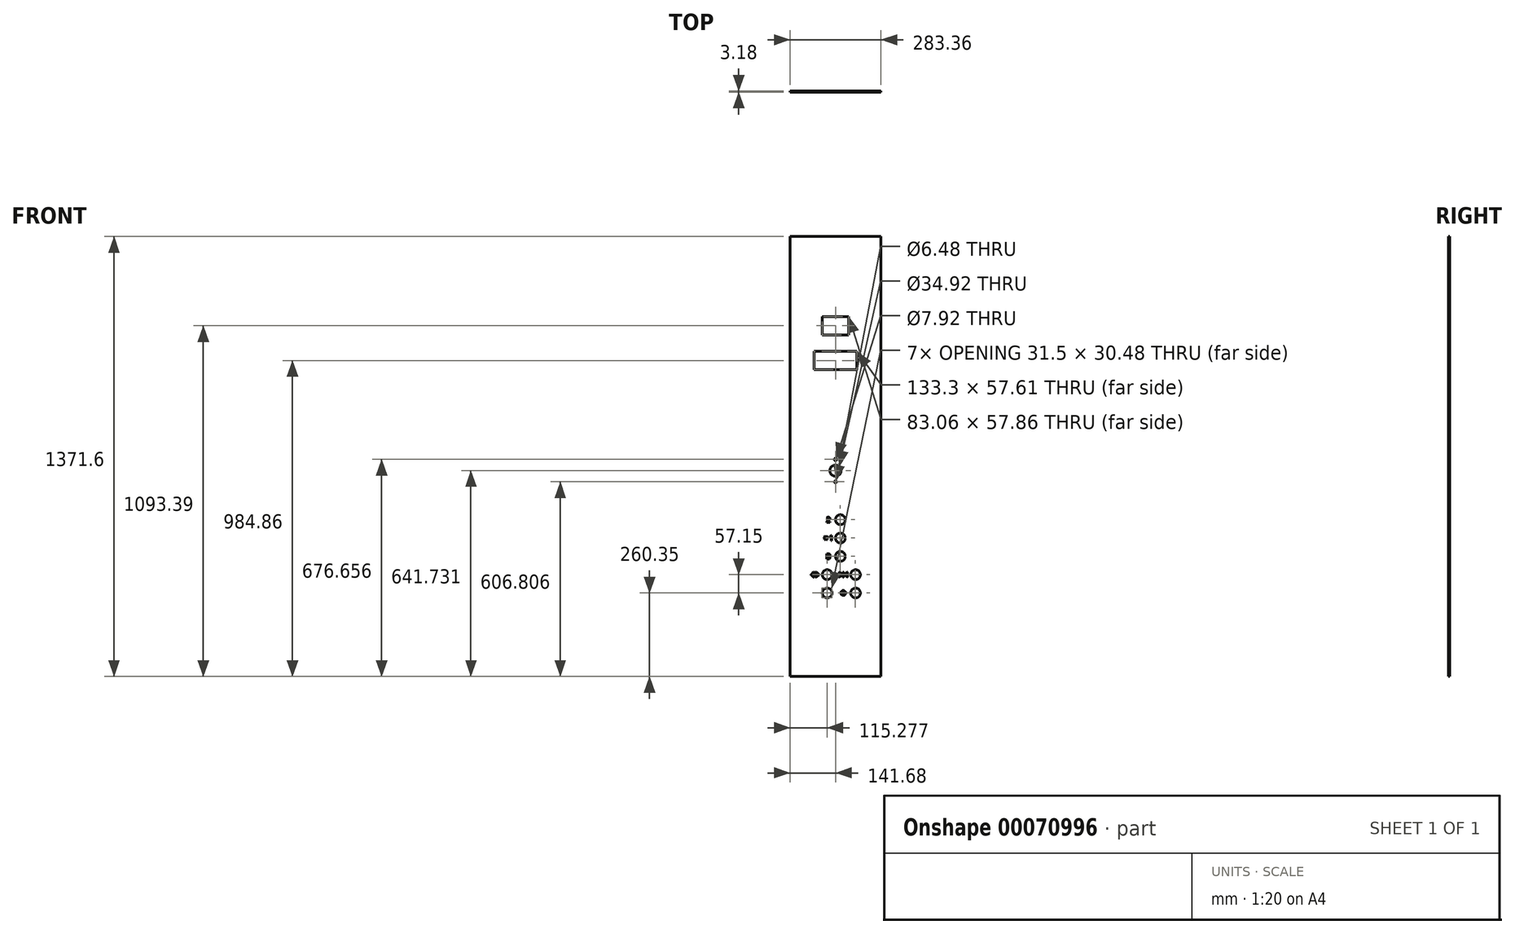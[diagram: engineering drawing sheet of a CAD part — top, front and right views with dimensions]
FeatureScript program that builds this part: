
annotation { "Feature Type Name" : "Feature", "Feature Type Description" : "" }
export const myFeature = defineFeature(function(context is Context, id is Id, definition is map)
    precondition{}
    {
        {
            var Q0;
            Q0=qCreatedBy(makeId("Front.planeOp"),FACE);
            var sketch = newSketch(context, id + "F0", { "sketchPlane" : qUnion([Q0])});
            skLineSegment(sketch, "E0.bottom", {"start": v(-141.68, 0) * mm, "end": v(141.68, 0) * mm});
            skLineSegment(sketch, "E0.top", {"start": v(-141.68, -1371.6) * mm, "end": v(141.68, -1371.6) * mm});
            skLineSegment(sketch, "E0.left", {"start": v(-141.68, 0) * mm, "end": v(-141.68, -1371.6) * mm});
            skLineSegment(sketch, "E0.right", {"start": v(141.68, 0) * mm, "end": v(141.68, -1371.6) * mm});
            skLineSegment(sketch, "E1", {"start": v(0, 0) * mm, "end": v(0, -1371.6) * mm, "construction": true});
            skLineSegment(sketch, "E2.bottom", {"start": v(-41.53, -249.28) * mm, "end": v(41.53, -249.28) * mm});
            skLineSegment(sketch, "E2.top", {"start": v(-41.53, -307.14) * mm, "end": v(41.53, -307.14) * mm});
            skLineSegment(sketch, "E2.left", {"start": v(-41.53, -249.28) * mm, "end": v(-41.53, -307.14) * mm});
            skLineSegment(sketch, "E2.right", {"start": v(41.53, -249.28) * mm, "end": v(41.53, -307.14) * mm});
            skLineSegment(sketch, "E3.bottom", {"start": v(-66.65, -357.94) * mm, "end": v(66.65, -357.94) * mm});
            skLineSegment(sketch, "E3.top", {"start": v(-66.65, -415.54) * mm, "end": v(66.65, -415.54) * mm});
            skLineSegment(sketch, "E3.left", {"start": v(-66.65, -357.94) * mm, "end": v(-66.65, -415.54) * mm});
            skLineSegment(sketch, "E3.right", {"start": v(66.65, -357.94) * mm, "end": v(66.65, -415.54) * mm});
            skArc(sketch, "E4", {"start": v(0.05, -883.86) * mm, "mid": v(30.5, -882.65) * mm, "end": v(0.05, -881.44) * mm});
            skPoint(sketch, "E5", {"position": v(0, -249.28) * mm});
            skPoint(sketch, "E6", {"position": v(0, -357.94) * mm});
            skArc(sketch, "E7", {"start": v(-0.16, -881.67) * mm, "mid": v(-1, -882.65) * mm, "end": v(-0.16, -883.63) * mm});
            skLineSegment(sketch, "E8", {"start": v(15.25, -882.65) * mm, "end": v(0, -882.65) * mm, "construction": true});
            skPoint(sketch, "E9.visualSharp", {"position": v(0.03, -881.66) * mm});
            skArc(sketch, "E9.filletArc", {"start": v(-0.16, -881.67) * mm, "mid": v(-0.02, -881.6) * mm, "end": v(0.05, -881.44) * mm});
            skPoint(sketch, "E10.visualSharp", {"position": v(0.03, -883.64) * mm});
            skArc(sketch, "E10.filletArc", {"start": v(0.05, -883.86) * mm, "mid": v(-0.02, -883.7) * mm, "end": v(-0.16, -883.63) * mm});
            skPoint(sketch, "E11.visualSharp", {"position": v(0.03, -940.8) * mm});
            skLineSegment(sketch, "E12", {"start": v(15.25, -939.8) * mm, "end": v(0, -939.8) * mm, "construction": true});
            skArc(sketch, "E13", {"start": v(0.05, -941) * mm, "mid": v(30.5, -939.8) * mm, "end": v(0.05, -938.6) * mm});
            skPoint(sketch, "E14.visualSharp", {"position": v(0.03, -938.8) * mm});
            skArc(sketch, "E14.filletArc", {"start": v(-0.16, -938.82) * mm, "mid": v(-0.02, -938.74) * mm, "end": v(0.05, -938.6) * mm});
            skArc(sketch, "E15", {"start": v(-0.16, -938.82) * mm, "mid": v(-1, -939.8) * mm, "end": v(-0.16, -940.78) * mm});
            skArc(sketch, "E11.filletArc", {"start": v(0.05, -941) * mm, "mid": v(-0.02, -940.86) * mm, "end": v(-0.16, -940.78) * mm});
            skPoint(sketch, "E16.visualSharp", {"position": v(0.03, -997.94) * mm});
            skLineSegment(sketch, "E17", {"start": v(15.25, -996.95) * mm, "end": v(0, -996.95) * mm, "construction": true});
            skArc(sketch, "E18", {"start": v(0.05, -998.16) * mm, "mid": v(30.5, -996.95) * mm, "end": v(0.05, -995.74) * mm});
            skPoint(sketch, "E19.visualSharp", {"position": v(0.03, -995.96) * mm});
            skArc(sketch, "E19.filletArc", {"start": v(-0.16, -995.97) * mm, "mid": v(-0.02, -995.9) * mm, "end": v(0.05, -995.74) * mm});
            skArc(sketch, "E20", {"start": v(-0.16, -995.97) * mm, "mid": v(-1, -996.95) * mm, "end": v(-0.16, -997.93) * mm});
            skArc(sketch, "E16.filletArc", {"start": v(0.05, -998.16) * mm, "mid": v(-0.02, -998) * mm, "end": v(-0.16, -997.93) * mm});
            skPoint(sketch, "E21.visualSharp", {"position": v(47.16, -1055.1) * mm});
            skLineSegment(sketch, "E22", {"start": v(62.38, -1054.1) * mm, "end": v(47.13, -1054.1) * mm, "construction": true});
            skArc(sketch, "E23", {"start": v(47.18, -1055.3) * mm, "mid": v(77.64, -1054.1) * mm, "end": v(47.18, -1052.9) * mm});
            skPoint(sketch, "E24.visualSharp", {"position": v(47.16, -1053.1) * mm});
            skArc(sketch, "E24.filletArc", {"start": v(46.97, -1053.12) * mm, "mid": v(47.11, -1053.04) * mm, "end": v(47.18, -1052.9) * mm});
            skArc(sketch, "E25", {"start": v(46.97, -1053.12) * mm, "mid": v(46.14, -1054.1) * mm, "end": v(46.97, -1055.08) * mm});
            skArc(sketch, "E21.filletArc", {"start": v(47.18, -1055.3) * mm, "mid": v(47.11, -1055.16) * mm, "end": v(46.97, -1055.08) * mm});
            skPoint(sketch, "E26.visualSharp", {"position": v(47.16, -1112.24) * mm});
            skLineSegment(sketch, "E27", {"start": v(62.38, -1111.25) * mm, "end": v(47.13, -1111.25) * mm, "construction": true});
            skArc(sketch, "E28", {"start": v(47.18, -1112.46) * mm, "mid": v(77.64, -1111.25) * mm, "end": v(47.18, -1110.04) * mm});
            skPoint(sketch, "E29.visualSharp", {"position": v(47.16, -1110.26) * mm});
            skArc(sketch, "E29.filletArc", {"start": v(46.97, -1110.27) * mm, "mid": v(47.11, -1110.2) * mm, "end": v(47.18, -1110.04) * mm});
            skArc(sketch, "E30", {"start": v(46.97, -1110.27) * mm, "mid": v(46.14, -1111.25) * mm, "end": v(46.97, -1112.23) * mm});
            skArc(sketch, "E26.filletArc", {"start": v(47.18, -1112.46) * mm, "mid": v(47.11, -1112.3) * mm, "end": v(46.97, -1112.23) * mm});
            skPoint(sketch, "E31.visualSharp", {"position": v(-41.13, -1055.1) * mm});
            skLineSegment(sketch, "E32", {"start": v(-25.9, -1054.1) * mm, "end": v(-41.16, -1054.1) * mm, "construction": true});
            skArc(sketch, "E33", {"start": v(-41.11, -1055.3) * mm, "mid": v(-10.66, -1054.1) * mm, "end": v(-41.11, -1052.9) * mm});
            skPoint(sketch, "E34.visualSharp", {"position": v(-41.13, -1053.1) * mm});
            skArc(sketch, "E34.filletArc", {"start": v(-41.32, -1053.12) * mm, "mid": v(-41.18, -1053.04) * mm, "end": v(-41.11, -1052.9) * mm});
            skArc(sketch, "E35", {"start": v(-41.32, -1053.12) * mm, "mid": v(-42.15, -1054.1) * mm, "end": v(-41.32, -1055.08) * mm});
            skArc(sketch, "E31.filletArc", {"start": v(-41.11, -1055.3) * mm, "mid": v(-41.18, -1055.16) * mm, "end": v(-41.32, -1055.08) * mm});
            skPoint(sketch, "E36.visualSharp", {"position": v(-41.13, -1112.24) * mm});
            skLineSegment(sketch, "E37", {"start": v(-25.9, -1111.25) * mm, "end": v(-41.16, -1111.25) * mm, "construction": true});
            skArc(sketch, "E38", {"start": v(-41.11, -1112.46) * mm, "mid": v(-10.66, -1111.25) * mm, "end": v(-41.11, -1110.04) * mm});
            skPoint(sketch, "E39.visualSharp", {"position": v(-41.13, -1110.26) * mm});
            skArc(sketch, "E39.filletArc", {"start": v(-41.32, -1110.27) * mm, "mid": v(-41.18, -1110.2) * mm, "end": v(-41.11, -1110.04) * mm});
            skArc(sketch, "E40", {"start": v(-41.32, -1110.27) * mm, "mid": v(-42.15, -1111.25) * mm, "end": v(-41.32, -1112.23) * mm});
            skArc(sketch, "E36.filletArc", {"start": v(-41.11, -1112.46) * mm, "mid": v(-41.18, -1112.3) * mm, "end": v(-41.32, -1112.23) * mm});
            skLineSegment(sketch, "E41.bottom", {"start": v(-141.68, -154.03) * mm, "end": v(141.68, -154.03) * mm, "construction": true});
            skLineSegment(sketch, "E41.top", {"start": v(-141.68, -1186.69) * mm, "end": v(141.68, -1186.69) * mm, "construction": true});
            skLineSegment(sketch, "E41.left", {"start": v(-141.68, -154.03) * mm, "end": v(-141.68, -1186.69) * mm, "construction": true});
            skLineSegment(sketch, "E41.right", {"start": v(141.68, -154.03) * mm, "end": v(141.68, -1186.69) * mm, "construction": true});
            skLineSegment(sketch, "E42", {"start": v(0, -154.03) * mm, "end": v(0, -1186.69) * mm, "construction": true});
            skCircle(sketch, "E43", {"center": v(0, -694.94) * mm, "radius": 3.96 * mm});
            skCircle(sketch, "E44", {"center": v(0, -729.87) * mm, "radius": 17.46 * mm});
            skCircle(sketch, "E45", {"center": v(0, -764.8) * mm, "radius": 3.24 * mm});
            skCircle(sketch, "E46", {"center": v(0, -806.07) * mm, "radius": 25.4 * mm, "construction": true});
            skText(sketch, "E47", { "text": "2", "fontName": "DroidSansMono.ttf"});
            skText(sketch, "E48", { "text": " 1", "fontName": "DroidSansMono.ttf"});
            skText(sketch, "E49", { "text": "B", "fontName": "DroidSansMono.ttf"});
            skLineSegment(sketch, "E50", {"start": v(-28.69, -882.65) * mm, "end": v(-17, -882.65) * mm, "construction": true});
            skCircle(sketch, "E51", {"center": v(-29.89, -939.8) * mm, "radius": 2.49 * mm, "construction": true});
            skLineSegment(sketch, "E52", {"start": v(-31.7, -937.31) * mm, "end": v(-28.08, -937.31) * mm, "construction": true});
            skLineSegment(sketch, "E53", {"start": v(-28.08, -937.31) * mm, "end": v(-26.96, -940.75) * mm, "construction": true});
            skLineSegment(sketch, "E54", {"start": v(-26.96, -940.75) * mm, "end": v(-29.89, -942.88) * mm, "construction": true});
            skLineSegment(sketch, "E55", {"start": v(-29.89, -942.88) * mm, "end": v(-32.81, -940.75) * mm, "construction": true});
            skLineSegment(sketch, "E56", {"start": v(-32.81, -940.75) * mm, "end": v(-31.7, -937.31) * mm, "construction": true});
            skLineSegment(sketch, "E57", {"start": v(-31.7, -937.31) * mm, "end": v(-29.89, -931.75) * mm});
            skLineSegment(sketch, "E58", {"start": v(-28.08, -937.31) * mm, "end": v(-29.89, -931.75) * mm});
            skLineSegment(sketch, "E59", {"start": v(-28.08, -937.31) * mm, "end": v(-22.23, -937.31) * mm});
            skLineSegment(sketch, "E60", {"start": v(-26.96, -940.75) * mm, "end": v(-22.23, -937.31) * mm});
            skLineSegment(sketch, "E61", {"start": v(-29.89, -942.88) * mm, "end": v(-25.16, -946.31) * mm});
            skLineSegment(sketch, "E62", {"start": v(-26.96, -940.75) * mm, "end": v(-25.16, -946.31) * mm});
            skLineSegment(sketch, "E63", {"start": v(-29.89, -942.88) * mm, "end": v(-34.62, -946.31) * mm});
            skLineSegment(sketch, "E64", {"start": v(-32.81, -940.75) * mm, "end": v(-34.62, -946.31) * mm});
            skLineSegment(sketch, "E65", {"start": v(-31.7, -937.31) * mm, "end": v(-37.55, -937.31) * mm});
            skLineSegment(sketch, "E66", {"start": v(-32.81, -940.75) * mm, "end": v(-37.55, -937.31) * mm});
            skCircle(sketch, "E67", {"center": v(-29.89, -939.8) * mm, "radius": 8.05 * mm, "construction": true});
            const initialGuessF0  = {"E47": [-0.02869, -0.8907, 1, 0, 0.0161], "E48": [-0.0337, -0.94785, 1, 0, 0.0161], "E49": [-0.02906, -1.005, 1, 0, 0.0161]};
            skSetInitialGuess(sketch, initialGuessF0);
            skSolve(sketch);
        }
        {
            var Q0;
            Q0=makeQuery(id+"F0.imprint","IMPRINT",FACE,{"disambiguationData":[TD([[makeQuery(id+"F0.imprint","IMPRINT",EDGE,{"derivedFrom":sQuery(id+"F0.wireOp",EDGE,"E0.bottom")}),-1.0]])]});
            var Q1;
            Q1=makeQuery(id+"F0.imprint","IMPRINT",FACE,{"disambiguationData":[TD([[makeQuery(id+"F0.imprint","IMPRINT",EDGE,{"derivedFrom":sQuery(id+"F0.wireOp",EDGE,"E49.sketch_text.stroke-11")}),1.0]])]});
            var Q2;
            Q2=makeQuery(id+"F0.imprint","IMPRINT",FACE,{"disambiguationData":[TD([[makeQuery(id+"F0.imprint","IMPRINT",EDGE,{"derivedFrom":sQuery(id+"F0.wireOp",EDGE,"E49.sketch_text.stroke-18")}),1.0]])]});
            extrude(context, id + "F1", {"entities" : qUnion([Q0, Q1, Q2]), "depth" : 3.17 * mm});
        }
        {
            var Q0;
            Q0=makeQuery(id+"F0.imprint","IMPRINT",FACE,{"disambiguationData":[TD([[makeQuery(id+"F0.imprint","IMPRINT",EDGE,{"derivedFrom":sQuery(id+"F0.wireOp",EDGE,"E49.sketch_text.stroke-0")}),-1.0]])]});
            var Q1;
            Q1=makeQuery(id+"F0.imprint","IMPRINT",FACE,{"disambiguationData":[TD([[makeQuery(id+"F0.imprint","IMPRINT",EDGE,{"derivedFrom":sQuery(id+"F0.wireOp",EDGE,"E57")}),-1.0]])]});
            var Q2;
            Q2=makeQuery(id+"F0.imprint","IMPRINT",FACE,{"disambiguationData":[TD([[makeQuery(id+"F0.imprint","IMPRINT",EDGE,{"derivedFrom":sQuery(id+"F0.wireOp",EDGE,"E48.sketch_text.stroke-0")}),-1.0]])]});
            var Q3;
            Q3=makeQuery(id+"F0.imprint","IMPRINT",FACE,{"disambiguationData":[TD([[makeQuery(id+"F0.imprint","IMPRINT",EDGE,{"derivedFrom":sQuery(id+"F0.wireOp",EDGE,"E47.sketch_text.stroke-0")}),-1.0]])]});
            extrude(context, id + "F2", {"entities" : qUnion([Q0, Q1, Q2, Q3]), "operationType" : NewBodyOperationType.ADD, "depth" : 2.92 * mm});
        }
        {
            var Q0;
            Q0=makeQuery(id+"F1.opExtrude","CAP_FACE",FACE,{"disambiguationData":[OSD([sQuery(id+"F0.wireOp",EDGE,"E0.bottom"),sQuery(id+"F0.wireOp",EDGE,"E0.top"),sQuery(id+"F0.wireOp",EDGE,"E0.left"),sQuery(id+"F0.wireOp",EDGE,"E0.right"),sQuery(id+"F0.wireOp",EDGE,"E2.bottom"),sQuery(id+"F0.wireOp",EDGE,"E2.top"),sQuery(id+"F0.wireOp",EDGE,"E2.left"),sQuery(id+"F0.wireOp",EDGE,"E2.right"),sQuery(id+"F0.wireOp",EDGE,"E3.bottom"),sQuery(id+"F0.wireOp",EDGE,"E3.top"),sQuery(id+"F0.wireOp",EDGE,"E3.left"),sQuery(id+"F0.wireOp",EDGE,"E3.right"),sQuery(id+"F0.wireOp",EDGE,"E4"),sQuery(id+"F0.wireOp",EDGE,"E7"),sQuery(id+"F0.wireOp",EDGE,"E9.filletArc"),sQuery(id+"F0.wireOp",EDGE,"E10.filletArc"),sQuery(id+"F0.wireOp",EDGE,"E13"),sQuery(id+"F0.wireOp",EDGE,"E14.filletArc"),sQuery(id+"F0.wireOp",EDGE,"E15"),sQuery(id+"F0.wireOp",EDGE,"E11.filletArc"),sQuery(id+"F0.wireOp",EDGE,"E18"),sQuery(id+"F0.wireOp",EDGE,"E19.filletArc"),sQuery(id+"F0.wireOp",EDGE,"E20"),sQuery(id+"F0.wireOp",EDGE,"E16.filletArc"),sQuery(id+"F0.wireOp",EDGE,"E23"),sQuery(id+"F0.wireOp",EDGE,"E24.filletArc"),sQuery(id+"F0.wireOp",EDGE,"E25"),sQuery(id+"F0.wireOp",EDGE,"E21.filletArc"),sQuery(id+"F0.wireOp",EDGE,"E28"),sQuery(id+"F0.wireOp",EDGE,"E29.filletArc"),sQuery(id+"F0.wireOp",EDGE,"E30"),sQuery(id+"F0.wireOp",EDGE,"E26.filletArc"),sQuery(id+"F0.wireOp",EDGE,"E33"),sQuery(id+"F0.wireOp",EDGE,"E34.filletArc"),sQuery(id+"F0.wireOp",EDGE,"E35"),sQuery(id+"F0.wireOp",EDGE,"E31.filletArc"),sQuery(id+"F0.wireOp",EDGE,"E38"),sQuery(id+"F0.wireOp",EDGE,"E39.filletArc"),sQuery(id+"F0.wireOp",EDGE,"E40"),sQuery(id+"F0.wireOp",EDGE,"E36.filletArc"),sQuery(id+"F0.wireOp",EDGE,"E43"),sQuery(id+"F0.wireOp",EDGE,"E44"),sQuery(id+"F0.wireOp",EDGE,"E45")])],"isStart":false});
            var sketch = newSketch(context, id + "F3", { "sketchPlane" : qUnion([Q0])});
            skText(sketch, "E68", { "text": "2", "fontName": "DroidSansMono.ttf"});
            skText(sketch, "E69", { "text": " 1", "fontName": "DroidSansMono.ttf"});
            skText(sketch, "E70", { "text": "B", "fontName": "DroidSansMono.ttf"});
            skLineSegment(sketch, "E71", {"start": v(-28.69, -882.65) * mm, "end": v(-17, -882.65) * mm, "construction": true});
            skCircle(sketch, "E72", {"center": v(-29.89, -939.8) * mm, "radius": 2.49 * mm, "construction": true});
            skLineSegment(sketch, "E73", {"start": v(-31.7, -937.31) * mm, "end": v(-28.08, -937.31) * mm, "construction": true});
            skLineSegment(sketch, "E74", {"start": v(-28.08, -937.31) * mm, "end": v(-26.96, -940.75) * mm, "construction": true});
            skLineSegment(sketch, "E75", {"start": v(-26.96, -940.75) * mm, "end": v(-29.89, -942.88) * mm, "construction": true});
            skLineSegment(sketch, "E76", {"start": v(-29.89, -942.88) * mm, "end": v(-32.81, -940.75) * mm, "construction": true});
            skLineSegment(sketch, "E77", {"start": v(-32.81, -940.75) * mm, "end": v(-31.7, -937.31) * mm, "construction": true});
            skLineSegment(sketch, "E78", {"start": v(-31.7, -937.31) * mm, "end": v(-29.89, -931.75) * mm});
            skLineSegment(sketch, "E79", {"start": v(-28.08, -937.31) * mm, "end": v(-29.89, -931.75) * mm});
            skLineSegment(sketch, "E80", {"start": v(-28.08, -937.31) * mm, "end": v(-22.23, -937.31) * mm});
            skLineSegment(sketch, "E81", {"start": v(-26.96, -940.75) * mm, "end": v(-22.23, -937.31) * mm});
            skLineSegment(sketch, "E82", {"start": v(-29.89, -942.88) * mm, "end": v(-25.16, -946.31) * mm});
            skLineSegment(sketch, "E83", {"start": v(-26.96, -940.75) * mm, "end": v(-25.16, -946.31) * mm});
            skLineSegment(sketch, "E84", {"start": v(-29.89, -942.88) * mm, "end": v(-34.62, -946.31) * mm});
            skLineSegment(sketch, "E85", {"start": v(-32.81, -940.75) * mm, "end": v(-34.62, -946.31) * mm});
            skLineSegment(sketch, "E86", {"start": v(-31.7, -937.31) * mm, "end": v(-37.55, -937.31) * mm});
            skLineSegment(sketch, "E87", {"start": v(-32.81, -940.75) * mm, "end": v(-37.55, -937.31) * mm});
            skCircle(sketch, "E88", {"center": v(-29.89, -939.8) * mm, "radius": 8.05 * mm, "construction": true});
            skLineSegment(sketch, "E89.bottom", {"start": v(-76.7, -1046.11) * mm, "end": v(-51.3, -1046.11) * mm, "construction": true});
            skLineSegment(sketch, "E89.top", {"start": v(-76.7, -1062.09) * mm, "end": v(-51.3, -1062.09) * mm, "construction": true});
            skLineSegment(sketch, "E89.left", {"start": v(-76.7, -1046.11) * mm, "end": v(-76.7, -1062.09) * mm, "construction": true});
            skLineSegment(sketch, "E89.right", {"start": v(-51.3, -1046.11) * mm, "end": v(-51.3, -1062.09) * mm, "construction": true});
            skLineSegment(sketch, "E90", {"start": v(-69.07, -1046.3) * mm, "end": v(-76.27, -1053.66) * mm});
            skLineSegment(sketch, "E91", {"start": v(-76.27, -1054.54) * mm, "end": v(-69.07, -1061.9) * mm});
            skLineSegment(sketch, "E92", {"start": v(-67.98, -1061.45) * mm, "end": v(-67.98, -1046.75) * mm});
            skLineSegment(sketch, "E93", {"start": v(-60.04, -1046.75) * mm, "end": v(-60.04, -1061.45) * mm});
            skLineSegment(sketch, "E94", {"start": v(-58.95, -1061.9) * mm, "end": v(-51.74, -1054.54) * mm});
            skLineSegment(sketch, "E95", {"start": v(-51.74, -1053.66) * mm, "end": v(-58.95, -1046.3) * mm});
            skLineSegment(sketch, "E96", {"start": v(-64.8, -1046.75) * mm, "end": v(-64.8, -1061.45) * mm});
            skLineSegment(sketch, "E97", {"start": v(-64.17, -1062.09) * mm, "end": v(-63.85, -1062.09) * mm});
            skLineSegment(sketch, "E98", {"start": v(-63.21, -1061.45) * mm, "end": v(-63.21, -1046.75) * mm});
            skLineSegment(sketch, "E99", {"start": v(-63.85, -1046.11) * mm, "end": v(-64.17, -1046.11) * mm});
            skLineSegment(sketch, "E100", {"start": v(-74.05, -1053.66) * mm, "end": v(-70.65, -1050.19) * mm});
            skLineSegment(sketch, "E101", {"start": v(-69.56, -1050.63) * mm, "end": v(-69.56, -1057.57) * mm});
            skLineSegment(sketch, "E102", {"start": v(-70.65, -1058.01) * mm, "end": v(-74.05, -1054.54) * mm});
            skLineSegment(sketch, "E103", {"start": v(-58.45, -1050.63) * mm, "end": v(-58.45, -1057.57) * mm});
            skLineSegment(sketch, "E104", {"start": v(-57.36, -1058.01) * mm, "end": v(-53.97, -1054.54) * mm});
            skLineSegment(sketch, "E105", {"start": v(-53.97, -1053.66) * mm, "end": v(-57.36, -1050.19) * mm});
            skLineSegment(sketch, "E106", {"start": v(-76.7, -1054.1) * mm, "end": v(-51.3, -1054.1) * mm, "construction": true});
            skPoint(sketch, "E107.visualSharp", {"position": v(-67.98, -1045.2) * mm});
            skArc(sketch, "E107.filletArc", {"start": v(-67.98, -1046.75) * mm, "mid": v(-68.37, -1046.16) * mm, "end": v(-69.07, -1046.3) * mm});
            skPoint(sketch, "E108.visualSharp", {"position": v(-69.56, -1049.08) * mm});
            skArc(sketch, "E108.filletArc", {"start": v(-69.56, -1050.63) * mm, "mid": v(-69.96, -1050.05) * mm, "end": v(-70.65, -1050.19) * mm});
            skPoint(sketch, "E109.visualSharp", {"position": v(-76.7, -1054.1) * mm});
            skArc(sketch, "E109.filletArc", {"start": v(-76.27, -1053.66) * mm, "mid": v(-76.45, -1054.1) * mm, "end": v(-76.27, -1054.54) * mm});
            skPoint(sketch, "E110.visualSharp", {"position": v(-74.49, -1054.1) * mm});
            skArc(sketch, "E110.filletArc", {"start": v(-74.05, -1053.66) * mm, "mid": v(-74.23, -1054.1) * mm, "end": v(-74.05, -1054.54) * mm});
            skPoint(sketch, "E111.visualSharp", {"position": v(-67.98, -1063) * mm});
            skArc(sketch, "E111.filletArc", {"start": v(-69.07, -1061.9) * mm, "mid": v(-68.37, -1062.04) * mm, "end": v(-67.98, -1061.45) * mm});
            skPoint(sketch, "E112.visualSharp", {"position": v(-69.56, -1059.12) * mm});
            skArc(sketch, "E112.filletArc", {"start": v(-70.65, -1058.01) * mm, "mid": v(-69.96, -1058.15) * mm, "end": v(-69.56, -1057.57) * mm});
            skPoint(sketch, "E113.visualSharp", {"position": v(-64.8, -1046.11) * mm});
            skArc(sketch, "E113.filletArc", {"start": v(-64.17, -1046.11) * mm, "mid": v(-64.62, -1046.3) * mm, "end": v(-64.8, -1046.75) * mm});
            skPoint(sketch, "E114.visualSharp", {"position": v(-63.21, -1046.11) * mm});
            skArc(sketch, "E114.filletArc", {"start": v(-63.21, -1046.75) * mm, "mid": v(-63.4, -1046.3) * mm, "end": v(-63.85, -1046.11) * mm});
            skPoint(sketch, "E115.visualSharp", {"position": v(-64.8, -1062.09) * mm});
            skArc(sketch, "E115.filletArc", {"start": v(-64.8, -1061.45) * mm, "mid": v(-64.62, -1061.9) * mm, "end": v(-64.17, -1062.09) * mm});
            skPoint(sketch, "E116.visualSharp", {"position": v(-63.21, -1062.09) * mm});
            skArc(sketch, "E116.filletArc", {"start": v(-63.85, -1062.09) * mm, "mid": v(-63.4, -1061.9) * mm, "end": v(-63.21, -1061.45) * mm});
            skPoint(sketch, "E117.visualSharp", {"position": v(-60.04, -1063) * mm});
            skArc(sketch, "E117.filletArc", {"start": v(-60.04, -1061.45) * mm, "mid": v(-59.64, -1062.04) * mm, "end": v(-58.95, -1061.9) * mm});
            skPoint(sketch, "E118.visualSharp", {"position": v(-58.45, -1059.12) * mm});
            skArc(sketch, "E118.filletArc", {"start": v(-58.45, -1057.57) * mm, "mid": v(-58.06, -1058.15) * mm, "end": v(-57.36, -1058.01) * mm});
            skPoint(sketch, "E119.visualSharp", {"position": v(-58.45, -1049.08) * mm});
            skArc(sketch, "E119.filletArc", {"start": v(-57.36, -1050.19) * mm, "mid": v(-58.06, -1050.05) * mm, "end": v(-58.45, -1050.63) * mm});
            skPoint(sketch, "E120.visualSharp", {"position": v(-60.04, -1045.2) * mm});
            skArc(sketch, "E120.filletArc", {"start": v(-58.95, -1046.3) * mm, "mid": v(-59.64, -1046.16) * mm, "end": v(-60.04, -1046.75) * mm});
            skPoint(sketch, "E121.visualSharp", {"position": v(-51.3, -1054.1) * mm});
            skArc(sketch, "E121.filletArc", {"start": v(-51.74, -1054.54) * mm, "mid": v(-51.56, -1054.1) * mm, "end": v(-51.74, -1053.66) * mm});
            skPoint(sketch, "E122.visualSharp", {"position": v(-53.53, -1054.1) * mm});
            skArc(sketch, "E122.filletArc", {"start": v(-53.97, -1054.54) * mm, "mid": v(-53.79, -1054.1) * mm, "end": v(-53.97, -1053.66) * mm});
            skLineSegment(sketch, "E123", {"start": v(-72.35, -1051.92) * mm, "end": v(-73.48, -1050.81) * mm, "construction": true});
            skLineSegment(sketch, "E124", {"start": v(-69.56, -1050.63) * mm, "end": v(-67.98, -1050.63) * mm, "construction": true});
            skLineSegment(sketch, "E125", {"start": v(-55.66, -1051.92) * mm, "end": v(-54.53, -1050.81) * mm, "construction": true});
            skLineSegment(sketch, "E126", {"start": v(-64.8, -1046.75) * mm, "end": v(-63.21, -1046.75) * mm, "construction": true});
            skLineSegment(sketch, "E127", {"start": v(-60.04, -1050.63) * mm, "end": v(-58.45, -1050.63) * mm, "construction": true});
            skLineSegment(sketch, "E128", {"start": v(-67.98, -1046.75) * mm, "end": v(-64.8, -1046.75) * mm, "construction": true});
            skLineSegment(sketch, "E129", {"start": v(-63.21, -1046.75) * mm, "end": v(-60.04, -1046.75) * mm, "construction": true});
            skLineSegment(sketch, "E130", {"start": v(-64, -1046.11) * mm, "end": v(-64, -1062.09) * mm, "construction": true});
            skPoint(sketch, "E131.visualSharp", {"position": v(20.58, -1054.1) * mm});
            skLineSegment(sketch, "E132", {"start": v(36.98, -1061.45) * mm, "end": v(36.98, -1046.75) * mm});
            skPoint(sketch, "E133.visualSharp", {"position": v(35.4, -1049.02) * mm});
            skLineSegment(sketch, "E134", {"start": v(35.4, -1050.54) * mm, "end": v(35.4, -1057.66) * mm});
            skLineSegment(sketch, "E135", {"start": v(20.58, -1054.1) * mm, "end": v(27.98, -1054.1) * mm, "construction": true});
            skPoint(sketch, "E136.visualSharp", {"position": v(11.58, -1045.23) * mm});
            skPoint(sketch, "E137.visualSharp", {"position": v(35.4, -1059.18) * mm});
            skLineSegment(sketch, "E138", {"start": v(28.44, -1054.55) * mm, "end": v(35.9, -1061.9) * mm});
            skPoint(sketch, "E139.visualSharp", {"position": v(11.58, -1062.97) * mm});
            skPoint(sketch, "E140.visualSharp", {"position": v(27.98, -1054.1) * mm});
            skLineSegment(sketch, "E141", {"start": v(11.58, -1046.75) * mm, "end": v(11.58, -1061.45) * mm});
            skLineSegment(sketch, "E142", {"start": v(25.08, -1061.45) * mm, "end": v(25.08, -1046.75) * mm});
            skPoint(sketch, "E143.visualSharp", {"position": v(36.98, -1062.97) * mm});
            skPoint(sketch, "E144.visualSharp", {"position": v(13.17, -1049.02) * mm});
            skLineSegment(sketch, "E145", {"start": v(12.66, -1061.9) * mm, "end": v(20.12, -1054.55) * mm});
            skPoint(sketch, "E146.visualSharp", {"position": v(13.17, -1059.18) * mm});
            skPoint(sketch, "E147.visualSharp", {"position": v(30.24, -1054.1) * mm});
            skLineSegment(sketch, "E148", {"start": v(13.17, -1050.54) * mm, "end": v(13.17, -1057.66) * mm});
            skLineSegment(sketch, "E149", {"start": v(23.49, -1046.75) * mm, "end": v(23.49, -1061.45) * mm});
            skPoint(sketch, "E150.visualSharp", {"position": v(18.32, -1054.1) * mm});
            skPoint(sketch, "E151.visualSharp", {"position": v(23.49, -1060.36) * mm});
            skPoint(sketch, "E152.visualSharp", {"position": v(36.98, -1045.23) * mm});
            skPoint(sketch, "E153.visualSharp", {"position": v(25.08, -1060.36) * mm});
            skLineSegment(sketch, "E154", {"start": v(35.9, -1046.3) * mm, "end": v(28.44, -1053.65) * mm});
            skPoint(sketch, "E155.visualSharp", {"position": v(23.49, -1044.39) * mm});
            skLineSegment(sketch, "E156", {"start": v(20.12, -1053.65) * mm, "end": v(12.66, -1046.3) * mm});
            skPoint(sketch, "E157.visualSharp", {"position": v(25.08, -1044.39) * mm});
            skArc(sketch, "E146.filletArc", {"start": v(13.17, -1057.66) * mm, "mid": v(13.56, -1058.25) * mm, "end": v(14.25, -1058.11) * mm});
            skLineSegment(sketch, "E158", {"start": v(16.06, -1051.87) * mm, "end": v(17.17, -1050.74) * mm, "construction": true});
            skLineSegment(sketch, "E159", {"start": v(34.31, -1058.11) * mm, "end": v(30.7, -1054.55) * mm});
            skArc(sketch, "E137.filletArc", {"start": v(34.31, -1058.11) * mm, "mid": v(35, -1058.25) * mm, "end": v(35.4, -1057.66) * mm});
            skLineSegment(sketch, "E160", {"start": v(14.25, -1058.11) * mm, "end": v(17.86, -1054.55) * mm});
            skArc(sketch, "E140.filletArc", {"start": v(28.44, -1053.65) * mm, "mid": v(28.25, -1054.1) * mm, "end": v(28.44, -1054.55) * mm});
            skArc(sketch, "E150.filletArc", {"start": v(17.86, -1054.55) * mm, "mid": v(18.05, -1054.1) * mm, "end": v(17.86, -1053.65) * mm});
            skLineSegment(sketch, "E161", {"start": v(30.7, -1053.65) * mm, "end": v(34.31, -1050.09) * mm});
            skLineSegment(sketch, "E162", {"start": v(32.5, -1051.87) * mm, "end": v(31.4, -1050.74) * mm, "construction": true});
            skLineSegment(sketch, "E163", {"start": v(35.4, -1050.54) * mm, "end": v(36.98, -1050.54) * mm, "construction": true});
            skArc(sketch, "E133.filletArc", {"start": v(35.4, -1050.54) * mm, "mid": v(35, -1049.95) * mm, "end": v(34.31, -1050.09) * mm});
            skLineSegment(sketch, "E164", {"start": v(17.86, -1053.65) * mm, "end": v(14.25, -1050.09) * mm});
            skArc(sketch, "E131.filletArc", {"start": v(20.12, -1054.55) * mm, "mid": v(20.31, -1054.1) * mm, "end": v(20.12, -1053.65) * mm});
            skArc(sketch, "E147.filletArc", {"start": v(30.7, -1053.65) * mm, "mid": v(30.51, -1054.1) * mm, "end": v(30.7, -1054.55) * mm});
            skArc(sketch, "E144.filletArc", {"start": v(14.25, -1050.09) * mm, "mid": v(13.56, -1049.95) * mm, "end": v(13.17, -1050.54) * mm});
            skArc(sketch, "E143.filletArc", {"start": v(35.9, -1061.9) * mm, "mid": v(36.6, -1062.04) * mm, "end": v(36.98, -1061.45) * mm});
            skLineSegment(sketch, "E165", {"start": v(11.58, -1050.54) * mm, "end": v(13.17, -1050.54) * mm, "construction": true});
            skArc(sketch, "E139.filletArc", {"start": v(11.58, -1061.45) * mm, "mid": v(11.97, -1062.04) * mm, "end": v(12.66, -1061.9) * mm});
            skArc(sketch, "E136.filletArc", {"start": v(12.66, -1046.3) * mm, "mid": v(11.97, -1046.16) * mm, "end": v(11.58, -1046.75) * mm});
            skArc(sketch, "E151.filletArc", {"start": v(23.49, -1061.45) * mm, "mid": v(23.67, -1061.9) * mm, "end": v(24.12, -1062.09) * mm});
            skArc(sketch, "E153.filletArc", {"start": v(24.44, -1062.09) * mm, "mid": v(24.9, -1061.9) * mm, "end": v(25.08, -1061.45) * mm});
            skArc(sketch, "E152.filletArc", {"start": v(36.98, -1046.75) * mm, "mid": v(36.6, -1046.16) * mm, "end": v(35.9, -1046.3) * mm});
            skArc(sketch, "E157.filletArc", {"start": v(25.08, -1046.75) * mm, "mid": v(24.9, -1046.3) * mm, "end": v(24.44, -1046.11) * mm});
            skLineSegment(sketch, "E166", {"start": v(23.49, -1046.75) * mm, "end": v(25.08, -1046.75) * mm, "construction": true});
            skArc(sketch, "E155.filletArc", {"start": v(24.12, -1046.11) * mm, "mid": v(23.67, -1046.3) * mm, "end": v(23.49, -1046.75) * mm});
            skLineSegment(sketch, "E167", {"start": v(24.12, -1046.11) * mm, "end": v(24.44, -1046.11) * mm});
            skLineSegment(sketch, "E168", {"start": v(24.12, -1062.09) * mm, "end": v(24.44, -1062.09) * mm});
            skLineSegment(sketch, "E169", {"start": v(20.31, -1050.1) * mm, "end": v(20.31, -1055.92) * mm, "construction": true});
            skLineSegment(sketch, "E170", {"start": v(28.25, -1049.84) * mm, "end": v(28.25, -1055.9) * mm, "construction": true});
            skLineSegment(sketch, "E171", {"start": v(24.28, -1042.27) * mm, "end": v(24.28, -1076.34) * mm, "construction": true});
            skPoint(sketch, "E171.endSnap0", {"position": v(24.28, -1054.1) * mm});
            skLineSegment(sketch, "E172", {"start": v(11.58, -1054.1) * mm, "end": v(36.98, -1054.1) * mm, "construction": true});
            skCircle(sketch, "E173.cCircle", {"center": v(24.28, -1111.25) * mm, "radius": 7.99 * mm, "construction": true});
            skLineSegment(sketch, "E173.0", {"start": v(27.53, -1104.06) * mm, "end": v(31.48, -1108) * mm});
            skLineSegment(sketch, "E173.1", {"start": v(31.66, -1108.46) * mm, "end": v(31.66, -1114.04) * mm});
            skLineSegment(sketch, "E173.2", {"start": v(31.48, -1114.5) * mm, "end": v(27.53, -1118.44) * mm});
            skLineSegment(sketch, "E173.3", {"start": v(27.08, -1118.63) * mm, "end": v(21.49, -1118.63) * mm});
            skLineSegment(sketch, "E173.4", {"start": v(21.04, -1118.44) * mm, "end": v(17.09, -1114.5) * mm});
            skLineSegment(sketch, "E173.5", {"start": v(16.9, -1114.04) * mm, "end": v(16.9, -1108.46) * mm});
            skLineSegment(sketch, "E173.6", {"start": v(17.09, -1108) * mm, "end": v(21.04, -1104.06) * mm});
            skLineSegment(sketch, "E173.7", {"start": v(21.49, -1103.87) * mm, "end": v(27.08, -1103.87) * mm});
            skPoint(sketch, "E174.visualSharp", {"position": v(16.9, -1108.2) * mm});
            skArc(sketch, "E174.filletArc", {"start": v(17.09, -1108) * mm, "mid": v(16.95, -1108.21) * mm, "end": v(16.9, -1108.46) * mm});
            skPoint(sketch, "E175.visualSharp", {"position": v(21.23, -1103.87) * mm});
            skArc(sketch, "E175.filletArc", {"start": v(21.49, -1103.87) * mm, "mid": v(21.25, -1103.92) * mm, "end": v(21.04, -1104.06) * mm});
            skPoint(sketch, "E176.visualSharp", {"position": v(27.34, -1103.87) * mm});
            skArc(sketch, "E176.filletArc", {"start": v(27.53, -1104.06) * mm, "mid": v(27.32, -1103.92) * mm, "end": v(27.08, -1103.87) * mm});
            skPoint(sketch, "E177.visualSharp", {"position": v(31.66, -1108.2) * mm});
            skArc(sketch, "E177.filletArc", {"start": v(31.66, -1108.46) * mm, "mid": v(31.61, -1108.21) * mm, "end": v(31.48, -1108) * mm});
            skPoint(sketch, "E178.visualSharp", {"position": v(31.66, -1114.3) * mm});
            skArc(sketch, "E178.filletArc", {"start": v(31.48, -1114.5) * mm, "mid": v(31.61, -1114.29) * mm, "end": v(31.66, -1114.04) * mm});
            skPoint(sketch, "E179.visualSharp", {"position": v(27.34, -1118.63) * mm});
            skArc(sketch, "E179.filletArc", {"start": v(27.08, -1118.63) * mm, "mid": v(27.32, -1118.58) * mm, "end": v(27.53, -1118.44) * mm});
            skPoint(sketch, "E180.visualSharp", {"position": v(21.23, -1118.63) * mm});
            skArc(sketch, "E180.filletArc", {"start": v(21.04, -1118.44) * mm, "mid": v(21.25, -1118.58) * mm, "end": v(21.49, -1118.63) * mm});
            skPoint(sketch, "E181.visualSharp", {"position": v(16.9, -1114.3) * mm});
            skArc(sketch, "E181.filletArc", {"start": v(16.9, -1114.04) * mm, "mid": v(16.95, -1114.29) * mm, "end": v(17.09, -1114.5) * mm});
            skLineSegment(sketch, "E182.0", {"start": v(18.68, -1108.66) * mm, "end": v(21.7, -1105.64) * mm});
            skLineSegment(sketch, "E182.1", {"start": v(18.49, -1113.39) * mm, "end": v(18.49, -1109.11) * mm});
            skLineSegment(sketch, "E182.2", {"start": v(22.15, -1105.46) * mm, "end": v(26.42, -1105.46) * mm});
            skLineSegment(sketch, "E182.3", {"start": v(21.7, -1116.86) * mm, "end": v(18.68, -1113.84) * mm});
            skLineSegment(sketch, "E182.4", {"start": v(26.87, -1105.64) * mm, "end": v(29.89, -1108.66) * mm});
            skLineSegment(sketch, "E182.5", {"start": v(30.08, -1109.11) * mm, "end": v(30.08, -1113.39) * mm});
            skLineSegment(sketch, "E182.6", {"start": v(29.89, -1113.84) * mm, "end": v(26.87, -1116.86) * mm});
            skLineSegment(sketch, "E182.7", {"start": v(26.42, -1117.04) * mm, "end": v(22.15, -1117.04) * mm});
            skPoint(sketch, "E183.visualSharp", {"position": v(21.88, -1105.46) * mm});
            skArc(sketch, "E183.filletArc", {"start": v(22.15, -1105.46) * mm, "mid": v(21.9, -1105.5) * mm, "end": v(21.7, -1105.64) * mm});
            skPoint(sketch, "E184.visualSharp", {"position": v(30.08, -1108.85) * mm});
            skArc(sketch, "E184.filletArc", {"start": v(30.08, -1109.11) * mm, "mid": v(30.03, -1108.87) * mm, "end": v(29.89, -1108.66) * mm});
            skPoint(sketch, "E185.visualSharp", {"position": v(30.08, -1113.65) * mm});
            skArc(sketch, "E185.filletArc", {"start": v(29.89, -1113.84) * mm, "mid": v(30.03, -1113.63) * mm, "end": v(30.08, -1113.39) * mm});
            skPoint(sketch, "E186.visualSharp", {"position": v(26.68, -1117.04) * mm});
            skArc(sketch, "E186.filletArc", {"start": v(26.42, -1117.04) * mm, "mid": v(26.66, -1117) * mm, "end": v(26.87, -1116.86) * mm});
            skPoint(sketch, "E187.visualSharp", {"position": v(21.88, -1117.04) * mm});
            skArc(sketch, "E187.filletArc", {"start": v(21.7, -1116.86) * mm, "mid": v(21.9, -1117) * mm, "end": v(22.15, -1117.04) * mm});
            skPoint(sketch, "E188.visualSharp", {"position": v(18.49, -1113.65) * mm});
            skArc(sketch, "E188.filletArc", {"start": v(18.49, -1113.39) * mm, "mid": v(18.54, -1113.63) * mm, "end": v(18.68, -1113.84) * mm});
            skPoint(sketch, "E189.visualSharp", {"position": v(18.49, -1108.85) * mm});
            skArc(sketch, "E189.filletArc", {"start": v(18.68, -1108.66) * mm, "mid": v(18.54, -1108.87) * mm, "end": v(18.49, -1109.11) * mm});
            skLineSegment(sketch, "E190", {"start": v(21.6, -1109.33) * mm, "end": v(22.36, -1108.57) * mm});
            skLineSegment(sketch, "E191", {"start": v(22.72, -1108.57) * mm, "end": v(24.1, -1109.95) * mm});
            skLineSegment(sketch, "E192", {"start": v(24.46, -1109.95) * mm, "end": v(25.84, -1108.57) * mm});
            skLineSegment(sketch, "E193", {"start": v(26.2, -1108.57) * mm, "end": v(26.96, -1109.33) * mm});
            skLineSegment(sketch, "E194", {"start": v(26.96, -1109.7) * mm, "end": v(25.58, -1111.07) * mm});
            skLineSegment(sketch, "E195", {"start": v(25.58, -1111.43) * mm, "end": v(26.96, -1112.8) * mm});
            skLineSegment(sketch, "E196", {"start": v(26.96, -1113.17) * mm, "end": v(26.2, -1113.93) * mm});
            skLineSegment(sketch, "E197", {"start": v(25.84, -1113.93) * mm, "end": v(24.46, -1112.55) * mm});
            skLineSegment(sketch, "E198", {"start": v(24.1, -1112.55) * mm, "end": v(22.72, -1113.93) * mm});
            skLineSegment(sketch, "E199", {"start": v(22.36, -1113.93) * mm, "end": v(21.6, -1113.17) * mm});
            skLineSegment(sketch, "E200", {"start": v(21.6, -1112.8) * mm, "end": v(22.98, -1111.43) * mm});
            skLineSegment(sketch, "E201", {"start": v(22.98, -1111.07) * mm, "end": v(21.6, -1109.7) * mm});
            skLineSegment(sketch, "E202", {"start": v(23.16, -1111.25) * mm, "end": v(25.4, -1111.25) * mm, "construction": true});
            skLineSegment(sketch, "E203", {"start": v(24.28, -1110.13) * mm, "end": v(24.28, -1112.37) * mm, "construction": true});
            skPoint(sketch, "E204.visualSharp", {"position": v(21.42, -1109.51) * mm});
            skArc(sketch, "E204.filletArc", {"start": v(21.6, -1109.33) * mm, "mid": v(21.53, -1109.51) * mm, "end": v(21.6, -1109.7) * mm});
            skPoint(sketch, "E205.visualSharp", {"position": v(22.54, -1108.39) * mm});
            skArc(sketch, "E205.filletArc", {"start": v(22.72, -1108.57) * mm, "mid": v(22.54, -1108.5) * mm, "end": v(22.36, -1108.57) * mm});
            skPoint(sketch, "E206.visualSharp", {"position": v(23.16, -1111.25) * mm});
            skArc(sketch, "E206.filletArc", {"start": v(22.98, -1111.43) * mm, "mid": v(23.05, -1111.25) * mm, "end": v(22.98, -1111.07) * mm});
            skPoint(sketch, "E207.visualSharp", {"position": v(24.28, -1110.13) * mm});
            skArc(sketch, "E207.filletArc", {"start": v(24.1, -1109.95) * mm, "mid": v(24.28, -1110.02) * mm, "end": v(24.46, -1109.95) * mm});
            skPoint(sketch, "E208.visualSharp", {"position": v(26.02, -1108.39) * mm});
            skArc(sketch, "E208.filletArc", {"start": v(26.2, -1108.57) * mm, "mid": v(26.02, -1108.5) * mm, "end": v(25.84, -1108.57) * mm});
            skPoint(sketch, "E209.visualSharp", {"position": v(27.14, -1109.51) * mm});
            skArc(sketch, "E209.filletArc", {"start": v(26.96, -1109.7) * mm, "mid": v(27.04, -1109.51) * mm, "end": v(26.96, -1109.33) * mm});
            skPoint(sketch, "E210.visualSharp", {"position": v(25.4, -1111.25) * mm});
            skArc(sketch, "E210.filletArc", {"start": v(25.58, -1111.07) * mm, "mid": v(25.51, -1111.25) * mm, "end": v(25.58, -1111.43) * mm});
            skPoint(sketch, "E211.visualSharp", {"position": v(27.14, -1112.99) * mm});
            skArc(sketch, "E211.filletArc", {"start": v(26.96, -1113.17) * mm, "mid": v(27.04, -1112.99) * mm, "end": v(26.96, -1112.8) * mm});
            skPoint(sketch, "E212.visualSharp", {"position": v(26.02, -1114.11) * mm});
            skArc(sketch, "E212.filletArc", {"start": v(25.84, -1113.93) * mm, "mid": v(26.02, -1114) * mm, "end": v(26.2, -1113.93) * mm});
            skPoint(sketch, "E213.visualSharp", {"position": v(24.28, -1112.37) * mm});
            skArc(sketch, "E213.filletArc", {"start": v(24.46, -1112.55) * mm, "mid": v(24.28, -1112.48) * mm, "end": v(24.1, -1112.55) * mm});
            skPoint(sketch, "E214.visualSharp", {"position": v(22.54, -1114.11) * mm});
            skArc(sketch, "E214.filletArc", {"start": v(22.36, -1113.93) * mm, "mid": v(22.54, -1114) * mm, "end": v(22.72, -1113.93) * mm});
            skPoint(sketch, "E215.visualSharp", {"position": v(21.42, -1112.99) * mm});
            skArc(sketch, "E215.filletArc", {"start": v(21.6, -1112.8) * mm, "mid": v(21.53, -1112.99) * mm, "end": v(21.6, -1113.17) * mm});
            skCircle(sketch, "E216", {"center": v(24.28, -1111.25) * mm, "radius": 3.25 * mm, "construction": true});
            skPoint(sketch, "E217.visualSharp", {"position": v(26.68, -1105.46) * mm});
            skArc(sketch, "E217.filletArc", {"start": v(26.87, -1105.64) * mm, "mid": v(26.66, -1105.5) * mm, "end": v(26.42, -1105.46) * mm});
            skLineSegment(sketch, "E218.bottom", {"start": v(-71.63, -1103.26) * mm, "end": v(-56.39, -1103.26) * mm, "construction": true});
            skLineSegment(sketch, "E218.top", {"start": v(-71.63, -1119.24) * mm, "end": v(-56.39, -1119.24) * mm, "construction": true});
            skLineSegment(sketch, "E218.left", {"start": v(-71.63, -1103.26) * mm, "end": v(-71.63, -1119.24) * mm, "construction": true});
            skLineSegment(sketch, "E218.right", {"start": v(-56.39, -1103.26) * mm, "end": v(-56.39, -1119.24) * mm, "construction": true});
            skLineSegment(sketch, "E219", {"start": v(-71.63, -1111.25) * mm, "end": v(-56.39, -1111.25) * mm, "construction": true});
            skLineSegment(sketch, "E220", {"start": v(-64, -1119.24) * mm, "end": v(-64, -1103.26) * mm, "construction": true});
            skLineSegment(sketch, "E221", {"start": v(-62.9, -1118.6) * mm, "end": v(-56.9, -1118.6) * mm});
            skLineSegment(sketch, "E222", {"start": v(-64, -1117.02) * mm, "end": v(-61.75, -1117.02) * mm});
            skLineSegment(sketch, "E223", {"start": v(-60.53, -1115.42) * mm, "end": v(-62.78, -1107) * mm});
            skArc(sketch, "E224", {"start": v(-62.78, -1107) * mm, "mid": v(-63.23, -1106.32) * mm, "end": v(-64, -1106.06) * mm});
            skPoint(sketch, "E225.visualSharp", {"position": v(-60.1, -1117.02) * mm});
            skArc(sketch, "E225.filletArc", {"start": v(-61.75, -1117.02) * mm, "mid": v(-60.74, -1116.52) * mm, "end": v(-60.53, -1115.42) * mm});
            skArc(sketch, "E226", {"start": v(-64, -1119.24) * mm, "mid": v(-63.37, -1119.07) * mm, "end": v(-62.9, -1118.6) * mm});
            skArc(sketch, "E227", {"start": v(-63.25, -1103.9) * mm, "mid": v(-63.51, -1103.45) * mm, "end": v(-64, -1103.26) * mm});
            skArc(sketch, "E228", {"start": v(-61.25, -1106.59) * mm, "mid": v(-61.75, -1105.57) * mm, "end": v(-62.62, -1104.83) * mm});
            skLineSegment(sketch, "E229", {"start": v(-61.25, -1106.59) * mm, "end": v(-59, -1115) * mm});
            skArc(sketch, "E230", {"start": v(-56.4, -1117.96) * mm, "mid": v(-57.08, -1116.7) * mm, "end": v(-58.25, -1115.85) * mm});
            skPoint(sketch, "E231.visualSharp", {"position": v(-56.3, -1118.6) * mm});
            skArc(sketch, "E231.filletArc", {"start": v(-56.9, -1118.6) * mm, "mid": v(-56.5, -1118.4) * mm, "end": v(-56.4, -1117.96) * mm});
            skPoint(sketch, "E232.visualSharp", {"position": v(-63.44, -1104.53) * mm});
            skArc(sketch, "E232.filletArc", {"start": v(-63.25, -1103.9) * mm, "mid": v(-63.04, -1104.44) * mm, "end": v(-62.62, -1104.83) * mm});
            skPoint(sketch, "E233.visualSharp", {"position": v(-58.81, -1115.68) * mm});
            skArc(sketch, "E233.filletArc", {"start": v(-59, -1115) * mm, "mid": v(-58.72, -1115.51) * mm, "end": v(-58.25, -1115.85) * mm});
            skLineSegment(sketch, "E234", {"start": v(-60.53, -1115.42) * mm, "end": v(-59, -1115) * mm, "construction": true});
            skArc(sketch, "E235.MirrorCS", {"start": v(-64.76, -1103.9) * mm, "mid": v(-64.5, -1103.45) * mm, "end": v(-64, -1103.26) * mm});
            skArc(sketch, "E236.MirrorCS", {"start": v(-64.76, -1103.9) * mm, "mid": v(-64.97, -1104.44) * mm, "end": v(-65.4, -1104.83) * mm});
            skArc(sketch, "E237.MirrorCS", {"start": v(-66.77, -1106.59) * mm, "mid": v(-66.26, -1105.57) * mm, "end": v(-65.4, -1104.83) * mm});
            skLineSegment(sketch, "E238.MirrorCS", {"start": v(-66.77, -1106.59) * mm, "end": v(-69.02, -1115) * mm});
            skArc(sketch, "E239.MirrorCS", {"start": v(-69.02, -1115) * mm, "mid": v(-69.3, -1115.51) * mm, "end": v(-69.76, -1115.85) * mm});
            skArc(sketch, "E240.MirrorCS", {"start": v(-71.61, -1117.96) * mm, "mid": v(-70.93, -1116.7) * mm, "end": v(-69.76, -1115.85) * mm});
            skArc(sketch, "E241.MirrorCS", {"start": v(-71.12, -1118.6) * mm, "mid": v(-71.52, -1118.4) * mm, "end": v(-71.61, -1117.96) * mm});
            skLineSegment(sketch, "E242.MirrorCS", {"start": v(-65.1, -1118.6) * mm, "end": v(-71.12, -1118.6) * mm});
            skArc(sketch, "E243.MirrorCS", {"start": v(-64, -1119.24) * mm, "mid": v(-64.64, -1119.07) * mm, "end": v(-65.1, -1118.6) * mm});
            skLineSegment(sketch, "E244.MirrorCS", {"start": v(-64, -1117.02) * mm, "end": v(-66.26, -1117.02) * mm});
            skArc(sketch, "E245.MirrorCS", {"start": v(-66.26, -1117.02) * mm, "mid": v(-67.27, -1116.52) * mm, "end": v(-67.5, -1115.42) * mm});
            skLineSegment(sketch, "E246.MirrorCS", {"start": v(-67.5, -1115.42) * mm, "end": v(-65.23, -1107) * mm});
            skArc(sketch, "E247.MirrorCS", {"start": v(-65.23, -1107) * mm, "mid": v(-64.78, -1106.32) * mm, "end": v(-64, -1106.06) * mm});
            const initialGuessF3  = {"E68": [-0.02869, -0.8907, 1, 0, 0.0161], "E69": [-0.0337, -0.94785, 1, 0, 0.0161], "E70": [-0.02906, -1.005, 1, 0, 0.0161]};
            skSetInitialGuess(sketch, initialGuessF3);
            skSolve(sketch);
        }
        {
            var Q0;
            Q0=makeQuery(id+"F3.imprint","IMPRINT",FACE,{"disambiguationData":[TD([[makeQuery(id+"F3.imprint","IMPRINT",EDGE,{"derivedFrom":sQuery(id+"F3.wireOp",EDGE,"E90")}),1.0]])]});
            var Q1;
            Q1=makeQuery(id+"F3.imprint","IMPRINT",FACE,{"disambiguationData":[TD([[makeQuery(id+"F3.imprint","IMPRINT",EDGE,{"derivedFrom":sQuery(id+"F3.wireOp",EDGE,"E96")}),1.0]])]});
            var Q2;
            Q2=makeQuery(id+"F3.imprint","IMPRINT",FACE,{"disambiguationData":[TD([[makeQuery(id+"F3.imprint","IMPRINT",EDGE,{"derivedFrom":sQuery(id+"F3.wireOp",EDGE,"E93")}),1.0]])]});
            var Q3;
            Q3=makeQuery(id+"F3.imprint","IMPRINT",FACE,{"disambiguationData":[TD([[makeQuery(id+"F3.imprint","IMPRINT",EDGE,{"derivedFrom":sQuery(id+"F3.wireOp",EDGE,"E141")}),1.0]])]});
            var Q4;
            Q4=makeQuery(id+"F3.imprint","IMPRINT",FACE,{"disambiguationData":[TD([[makeQuery(id+"F3.imprint","IMPRINT",EDGE,{"derivedFrom":sQuery(id+"F3.wireOp",EDGE,"E142")}),1.0]])]});
            var Q5;
            Q5=makeQuery(id+"F3.imprint","IMPRINT",FACE,{"disambiguationData":[TD([[makeQuery(id+"F3.imprint","IMPRINT",EDGE,{"derivedFrom":sQuery(id+"F3.wireOp",EDGE,"E132")}),1.0]])]});
            var Q6;
            Q6=makeQuery(id+"F3.imprint","IMPRINT",FACE,{"disambiguationData":[TD([[makeQuery(id+"F3.imprint","IMPRINT",EDGE,{"derivedFrom":sQuery(id+"F3.wireOp",EDGE,"E190")}),-1.0]])]});
            var Q7;
            Q7=makeQuery(id+"F3.imprint","IMPRINT",FACE,{"disambiguationData":[TD([[makeQuery(id+"F3.imprint","IMPRINT",EDGE,{"derivedFrom":sQuery(id+"F3.wireOp",EDGE,"E173.0")}),-1.0]])]});
            var Q8;
            Q8=makeQuery(id+"F2.opExtrude","CAP_FACE",FACE,{"disambiguationData":[OSD([sQuery(id+"F0.wireOp",EDGE,"E57"),sQuery(id+"F0.wireOp",EDGE,"E58"),sQuery(id+"F0.wireOp",EDGE,"E59"),sQuery(id+"F0.wireOp",EDGE,"E60"),sQuery(id+"F0.wireOp",EDGE,"E61"),sQuery(id+"F0.wireOp",EDGE,"E62"),sQuery(id+"F0.wireOp",EDGE,"E63"),sQuery(id+"F0.wireOp",EDGE,"E64"),sQuery(id+"F0.wireOp",EDGE,"E65"),sQuery(id+"F0.wireOp",EDGE,"E66")])],"isStart":false});
            extrude(context, id + "F4", {"entities" : qUnion([Q0, Q1, Q2, Q3, Q4, Q5, Q6, Q7]), "operationType" : NewBodyOperationType.REMOVE, "endBound" : BoundingType.UP_TO_SURFACE, "oppositeDirection" : true, "endBoundEntityFace" : qUnion([Q8]), "depth" : 25.4 * mm});
        }
    });
